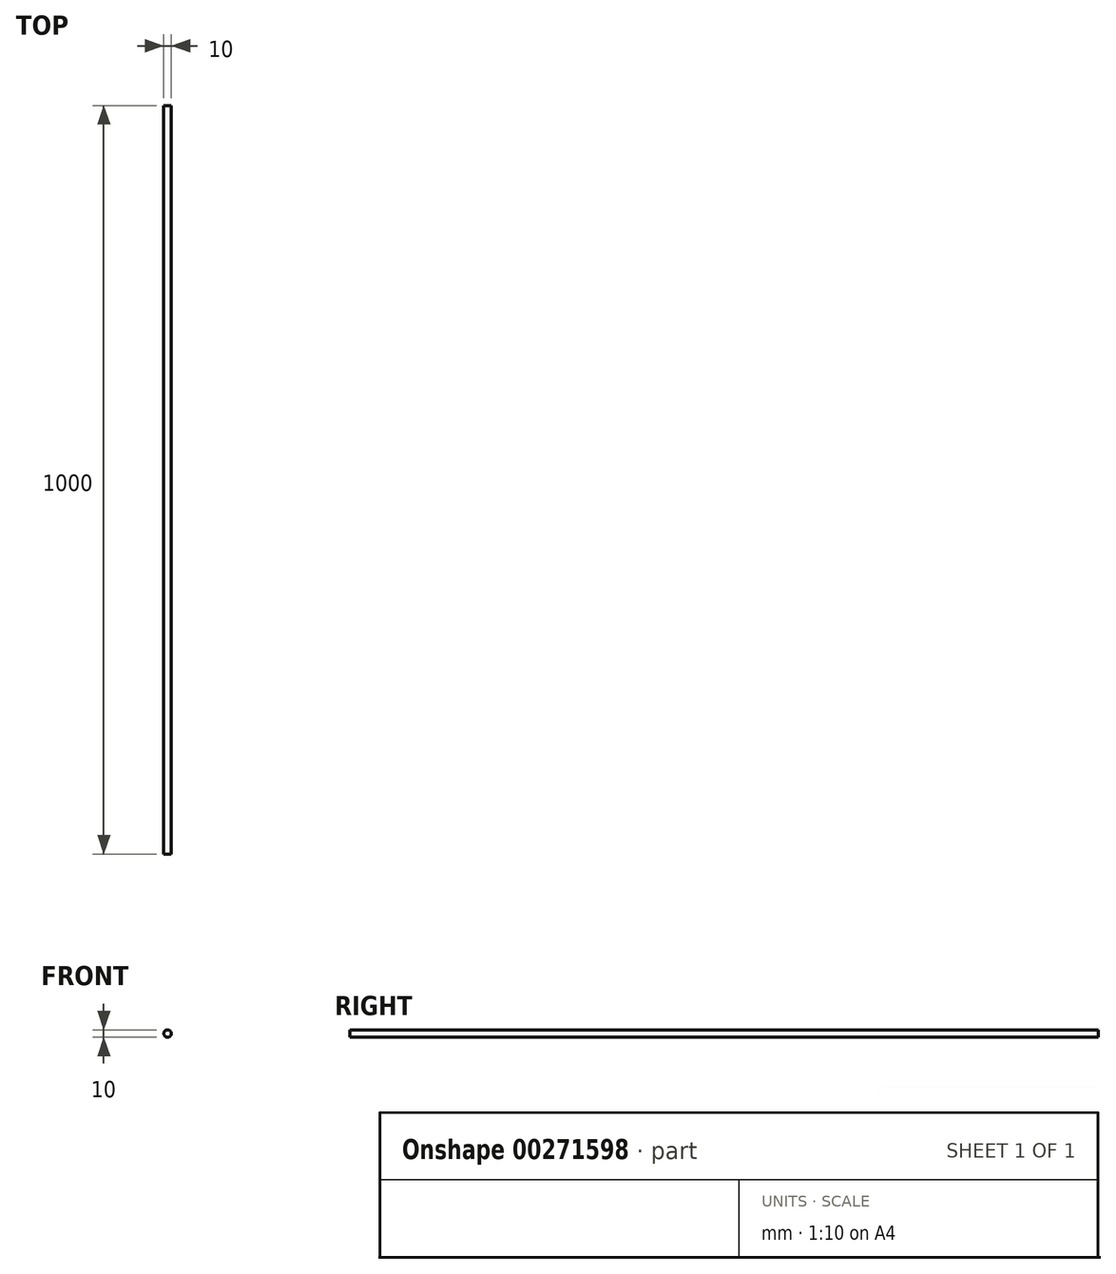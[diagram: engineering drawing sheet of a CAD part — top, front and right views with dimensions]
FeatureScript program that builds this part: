
annotation { "Feature Type Name" : "Feature", "Feature Type Description" : "" }
export const myFeature = defineFeature(function(context is Context, id is Id, definition is map)
    precondition{}
    {
        {
            var Q0;
            Q0=qCreatedBy(makeId("Front.planeOp"),FACE);
            var sketch = newSketch(context, id + "F0", { "sketchPlane" : qUnion([Q0])});
            skCircle(sketch, "E0", {"center": v(0, 0) * mm, "radius": 5 * mm});
            skSolve(sketch);
        }
        {
            var Q0;
            Q0 = qSketchRegion(id + "F0", true);
            extrude(context, id + "F1", {"entities" : qUnion([Q0]), "depth" : 1000 * mm});
        }
    });
